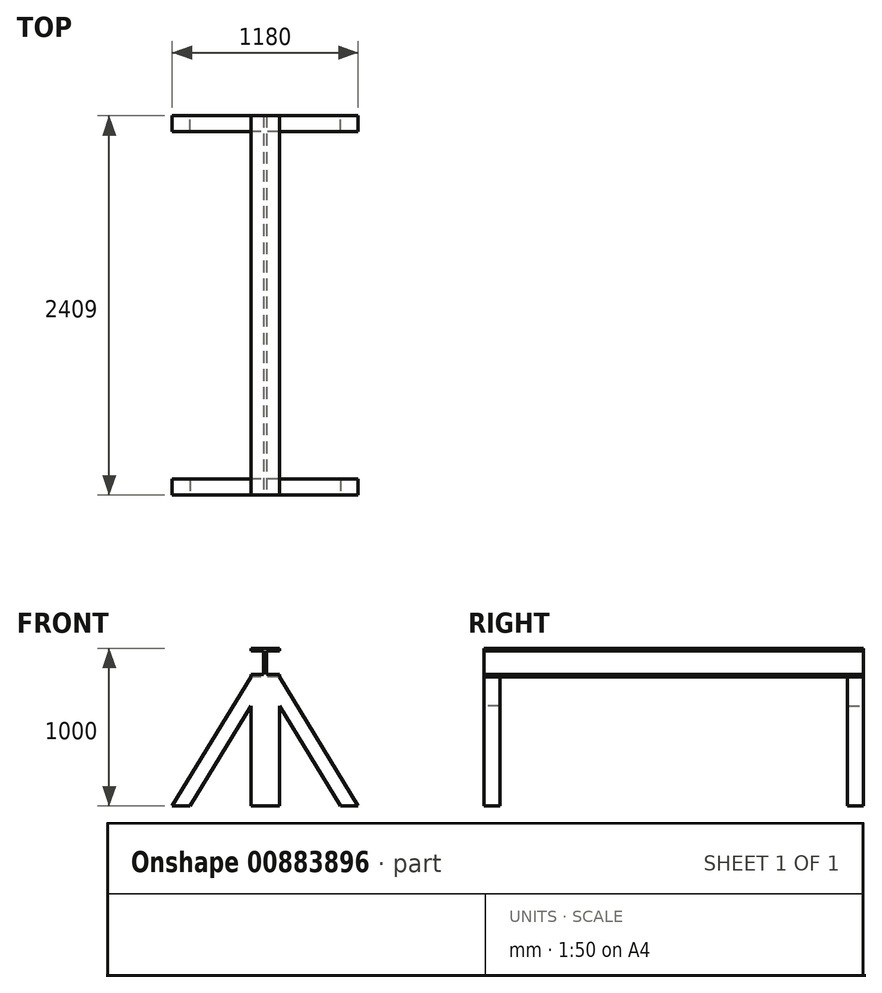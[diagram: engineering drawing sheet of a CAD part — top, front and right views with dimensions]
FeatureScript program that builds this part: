
annotation { "Feature Type Name" : "Feature", "Feature Type Description" : "" }
export const myFeature = defineFeature(function(context is Context, id is Id, definition is map)
    precondition{}
    {
        {
            var Q0;
            Q0=qCreatedBy(makeId("Front.planeOp"),FACE);
            var sketch = newSketch(context, id + "F0", { "sketchPlane" : qUnion([Q0])});
            skLineSegment(sketch, "E0.bottom", {"start": v(90, -90) * mm, "end": v(-90, -90) * mm});
            skLineSegment(sketch, "E0.top", {"start": v(90, 90) * mm, "end": v(-90, 90) * mm});
            skLineSegment(sketch, "E0.left", {"start": v(90, -90) * mm, "end": v(90, -75) * mm});
            skLineSegment(sketch, "E0.right", {"start": v(-90, -90) * mm, "end": v(-90, -75) * mm});
            skPoint(sketch, "E0.middle", {"position": v(0, 0) * mm});
            skLineSegment(sketch, "E1.bottom", {"start": v(-90, 75) * mm, "end": v(-10, 75) * mm});
            skLineSegment(sketch, "E1.top", {"start": v(-90, -75) * mm, "end": v(-10, -75) * mm});
            skLineSegment(sketch, "E1.right", {"start": v(-10, 75) * mm, "end": v(-10, -75) * mm});
            skLineSegment(sketch, "E2.bottom", {"start": v(90, 75) * mm, "end": v(10, 75) * mm});
            skLineSegment(sketch, "E2.top", {"start": v(90, -75) * mm, "end": v(10, -75) * mm});
            skLineSegment(sketch, "E2.right", {"start": v(10, 75) * mm, "end": v(10, -75) * mm});
            skLineSegment(sketch, "E3.trimOffspring", {"start": v(-90, 75) * mm, "end": v(-90, 90) * mm});
            skLineSegment(sketch, "E4.trimOffspring", {"start": v(90, 75) * mm, "end": v(90, 90) * mm});
            skSolve(sketch);
        }
        {
            var Q0;
            Q0 = qSketchRegion(id + "F0", true);
            extrude(context, id + "F1", {"entities" : qUnion([Q0]), "oppositeDirection" : true, "depth" : 2409 * mm, "offsetDistance" : 25 * mm});
        }
        {
            var Q0;
            Q0=qCreatedBy(makeId("Front.planeOp"),FACE);
            var sketch = newSketch(context, id + "F2", { "sketchPlane" : qUnion([Q0])});
            skLineSegment(sketch, "E5.0", {"start": v(90, -90) * mm, "end": v(-90, -90) * mm});
            skLineSegment(sketch, "E6.bottom", {"start": v(-90, -90) * mm, "end": v(90, -90) * mm});
            skLineSegment(sketch, "E6.top", {"start": v(-90, -910) * mm, "end": v(90, -910) * mm});
            skLineSegment(sketch, "E6.left", {"start": v(-90, -90) * mm, "end": v(-90, -910) * mm});
            skLineSegment(sketch, "E6.right", {"start": v(90, -90) * mm, "end": v(90, -910) * mm});
            skLineSegment(sketch, "E7", {"start": v(-90, -90) * mm, "end": v(-590, -910) * mm});
            skLineSegment(sketch, "E8", {"start": v(-590, -910) * mm, "end": v(-477.66, -910) * mm});
            skLineSegment(sketch, "E9", {"start": v(-477.66, -910) * mm, "end": v(-90, -274.24) * mm});
            skLineSegment(sketch, "E10.MirrorCS", {"start": v(590, -910) * mm, "end": v(477.66, -910) * mm});
            skLineSegment(sketch, "E11.MirrorCS", {"start": v(477.66, -910) * mm, "end": v(90, -274.24) * mm});
            skLineSegment(sketch, "E12.MirrorCS", {"start": v(90, -90) * mm, "end": v(590, -910) * mm});
            skSolve(sketch);
        }
        {
            var Q0;
            Q0 = qSketchRegion(id + "F2", true);
            extrude(context, id + "F3", {"entities" : qUnion([Q0]), "operationType" : NewBodyOperationType.ADD, "oppositeDirection" : true, "depth" : 100 * mm, "offsetDistance" : 25 * mm});
        }
        {
            var Q0;
            Q0=makeQuery(id+"F1.opExtrude","CAP_FACE",FACE,{"disambiguationData":[OSD([sQuery(id+"F0.wireOp",EDGE,"E0.bottom"),sQuery(id+"F0.wireOp",EDGE,"E0.top"),sQuery(id+"F0.wireOp",EDGE,"E0.left"),sQuery(id+"F0.wireOp",EDGE,"E0.right"),sQuery(id+"F0.wireOp",EDGE,"E1.bottom"),sQuery(id+"F0.wireOp",EDGE,"E1.top"),sQuery(id+"F0.wireOp",EDGE,"E1.right"),sQuery(id+"F0.wireOp",EDGE,"E2.bottom"),sQuery(id+"F0.wireOp",EDGE,"E2.top"),sQuery(id+"F0.wireOp",EDGE,"E2.right"),sQuery(id+"F0.wireOp",EDGE,"E3.trimOffspring"),sQuery(id+"F0.wireOp",EDGE,"E4.trimOffspring")])],"isStart":false});
            var sketch = newSketch(context, id + "F4", { "sketchPlane" : qUnion([Q0])});
            skLineSegment(sketch, "E13.0.0", {"start": v(90, -274.24) * mm, "end": v(477.66, -910) * mm});
            skLineSegment(sketch, "E13.0.1", {"start": v(477.66, -910) * mm, "end": v(590, -910) * mm});
            skLineSegment(sketch, "E13.0.2", {"start": v(590, -910) * mm, "end": v(90, -90) * mm});
            skLineSegment(sketch, "E13.0.3", {"start": v(90, -90) * mm, "end": v(-90, -90) * mm});
            skLineSegment(sketch, "E13.0.4", {"start": v(-90, -90) * mm, "end": v(-590, -910) * mm});
            skLineSegment(sketch, "E13.0.5", {"start": v(-590, -910) * mm, "end": v(-477.66, -910) * mm});
            skLineSegment(sketch, "E13.0.6", {"start": v(-477.66, -910) * mm, "end": v(-90, -274.24) * mm});
            skLineSegment(sketch, "E13.0.7", {"start": v(-90, -274.24) * mm, "end": v(-90, -910) * mm});
            skLineSegment(sketch, "E13.0.8", {"start": v(-90, -910) * mm, "end": v(90, -910) * mm});
            skLineSegment(sketch, "E13.0.9", {"start": v(90, -910) * mm, "end": v(90, -274.24) * mm});
            skSolve(sketch);
        }
        {
            var Q0;
            Q0 = qSketchRegion(id + "F4", true);
            extrude(context, id + "F5", {"entities" : qUnion([Q0]), "operationType" : NewBodyOperationType.ADD, "oppositeDirection" : true, "depth" : 100 * mm, "offsetDistance" : 25 * mm});
        }
    });
